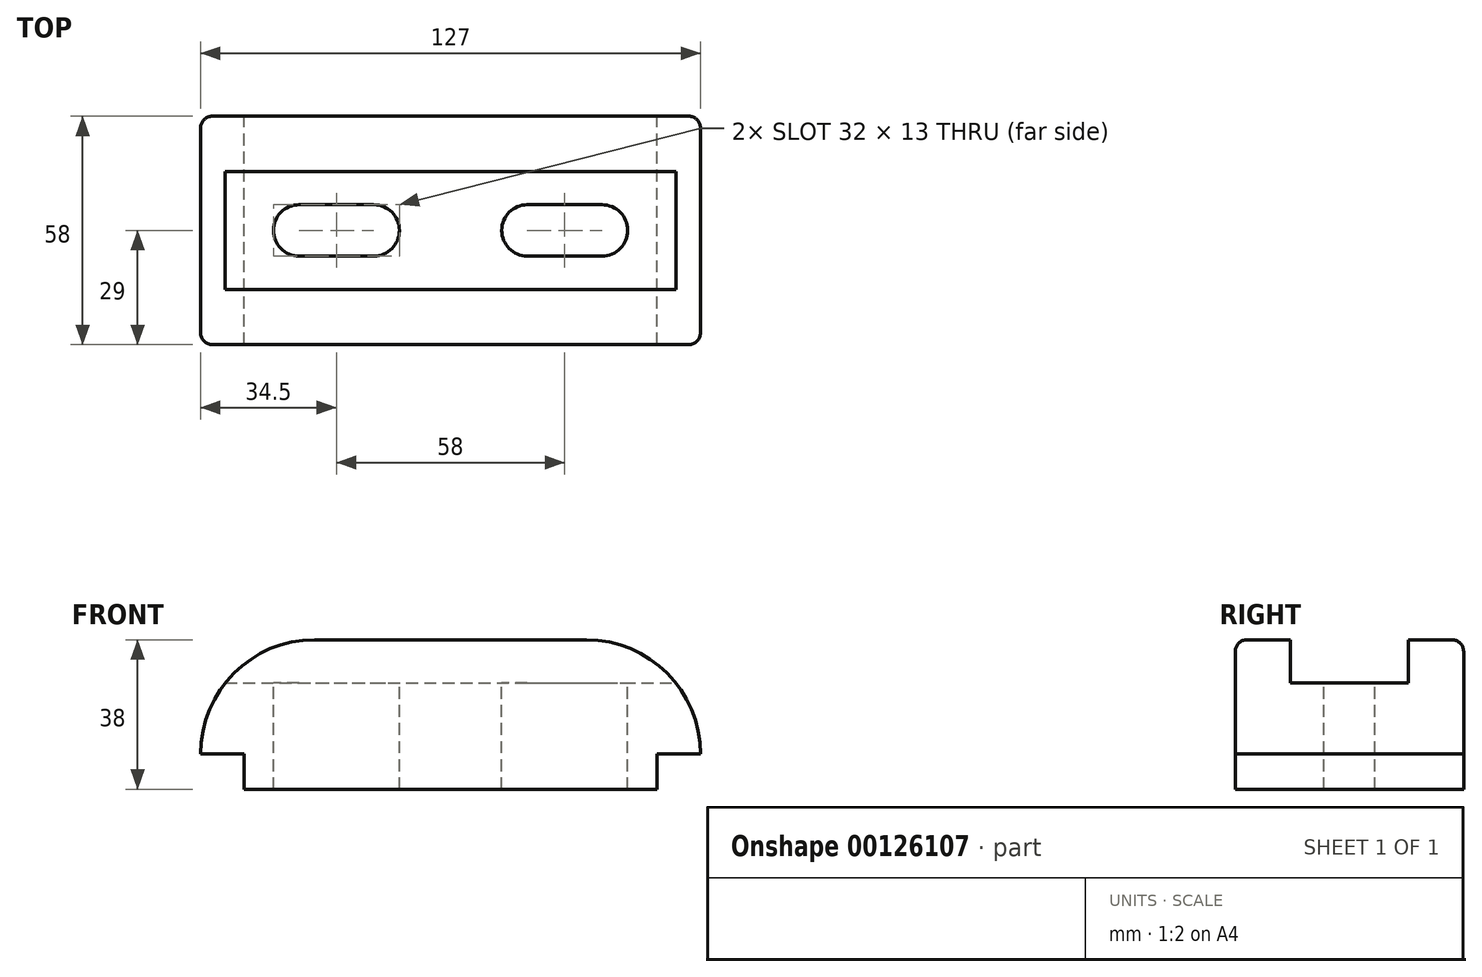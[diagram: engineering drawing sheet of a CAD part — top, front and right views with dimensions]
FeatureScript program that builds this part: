
annotation { "Feature Type Name" : "Feature", "Feature Type Description" : "" }
export const myFeature = defineFeature(function(context is Context, id is Id, definition is map)
    precondition{}
    {
        {
            var Q0;
            Q0=qCreatedBy(makeId("Front.planeOp"),FACE);
            var sketch = newSketch(context, id + "F0", { "sketchPlane" : qUnion([Q0])});
            skLineSegment(sketch, "E0", {"start": v(52.5, 0) * mm, "end": v(-52.5, 0) * mm});
            skLineSegment(sketch, "E1", {"start": v(-52.5, 0) * mm, "end": v(-52.5, 9) * mm});
            skLineSegment(sketch, "E2", {"start": v(-52.5, 9) * mm, "end": v(-63.5, 9) * mm});
            skLineSegment(sketch, "E3", {"start": v(52.5, 0) * mm, "end": v(52.5, 9) * mm});
            skLineSegment(sketch, "E4", {"start": v(52.5, 9) * mm, "end": v(63.5, 9) * mm});
            skArc(sketch, "E5", {"start": v(-34.5, 38) * mm, "mid": v(-55, 29.5) * mm, "end": v(-63.5, 9) * mm});
            skArc(sketch, "E6", {"start": v(63.5, 9) * mm, "mid": v(55, 29.5) * mm, "end": v(34.5, 38) * mm});
            skLineSegment(sketch, "E7", {"start": v(-34.5, 38) * mm, "end": v(34.5, 38) * mm});
            skSolve(sketch);
        }
        {
            var Q0;
            Q0=makeQuery(id+"F0.imprint","IMPRINT",FACE,{"disambiguationData":[TD([[makeQuery(id+"F0.imprint","IMPRINT",EDGE,{"derivedFrom":sQuery(id+"F0.wireOp",EDGE,"E0")}),-1.0]])]});
            extrude(context, id + "F1", {"entities" : qUnion([Q0]), "endBound" : BoundingType.SYMMETRIC, "depth" : 58 * mm});
        }
        {
            var Q0;
            Q0=makeQuery(id+"F1.opExtrude","CAP_EDGE",EDGE,{"disambiguationData":[OSD([sQuery(id+"F0.wireOp",EDGE,"E7")])],"isStart":false});
            var Q1;
            Q1=makeQuery(id+"F1.opExtrude","CAP_EDGE",EDGE,{"disambiguationData":[OSD([sQuery(id+"F0.wireOp",EDGE,"E7")])],"isStart":true});
            fillet(context, id + "F2", {"entities" : qUnion([Q0, Q1]), "radius" : 3 * mm, "tangentPropagation" : true, "allowEdgeOverflow" : false});
        }
        {
            var Q0;
            Q0=qCreatedBy(makeId("Right.planeOp"),FACE);
            var sketch = newSketch(context, id + "F3", { "sketchPlane" : qUnion([Q0])});
            skLineSegment(sketch, "E8.0", {"start": v(-26, 38) * mm, "end": v(26, 38) * mm});
            skLineSegment(sketch, "E9.bottom", {"start": v(15, 38) * mm, "end": v(-15, 38) * mm});
            skLineSegment(sketch, "E9.top", {"start": v(15, 27) * mm, "end": v(-15, 27) * mm});
            skLineSegment(sketch, "E9.left", {"start": v(15, 38) * mm, "end": v(15, 27) * mm});
            skLineSegment(sketch, "E9.right", {"start": v(-15, 38) * mm, "end": v(-15, 27) * mm});
            skSolve(sketch);
        }
        {
            var Q0;
            Q0 = qSketchRegion(id + "F3", true);
            extrude(context, id + "F4", {"entities" : qUnion([Q0]), "operationType" : NewBodyOperationType.REMOVE, "endBound" : BoundingType.THROUGH_ALL, "oppositeDirection" : true, "depth" : 25 * mm, "hasSecondDirection" : true, "secondDirectionBound" : SecondDirectionBoundingType.THROUGH_ALL, "secondDirectionOppositeDirection" : false, "secondDirectionDepth" : 25 * mm});
        }
        {
            var Q0;
            Q0=makeQuery(id+"F4.boolean.opBoolean","COPY",FACE,{"derivedFrom":makeQuery(id+"F4.opExtrude","SWEPT_FACE",FACE,{"disambiguationData":[OSD([sQuery(id+"F3.wireOp",EDGE,"E9.top")])]})});
            var sketch = newSketch(context, id + "F5", { "sketchPlane" : qUnion([Q0])});
            skLineSegment(sketch, "E10.1", {"start": v(-52.5, -29) * mm, "end": v(-52.5, 29) * mm});
            skLineSegment(sketch, "E10.2", {"start": v(52.5, -29) * mm, "end": v(52.5, 29) * mm});
            skArc(sketch, "E11", {"start": v(-38.5, 6.5) * mm, "mid": v(-45, 0) * mm, "end": v(-38.5, -6.5) * mm});
            skArc(sketch, "E12", {"start": v(-19.5, -6.5) * mm, "mid": v(-13, 0) * mm, "end": v(-19.5, 6.5) * mm});
            skArc(sketch, "E13", {"start": v(19.5, 6.5) * mm, "mid": v(13, 0) * mm, "end": v(19.5, -6.5) * mm});
            skArc(sketch, "E14", {"start": v(38.5, -6.5) * mm, "mid": v(45, 0) * mm, "end": v(38.5, 6.5) * mm});
            skLineSegment(sketch, "E15", {"start": v(-38.5, 6.5) * mm, "end": v(-19.5, 6.5) * mm});
            skLineSegment(sketch, "E16", {"start": v(-38.5, -6.5) * mm, "end": v(-19.5, -6.5) * mm});
            skLineSegment(sketch, "E17", {"start": v(19.5, 6.5) * mm, "end": v(38.5, 6.5) * mm});
            skLineSegment(sketch, "E18", {"start": v(19.5, -6.5) * mm, "end": v(38.5, -6.5) * mm});
            skSolve(sketch);
        }
        {
            var Q0;
            Q0 = qSketchRegion(id + "F5", true);
            extrude(context, id + "F6", {"entities" : qUnion([Q0]), "operationType" : NewBodyOperationType.REMOVE, "endBound" : BoundingType.THROUGH_ALL, "oppositeDirection" : true, "depth" : 25 * mm});
        }
    });
